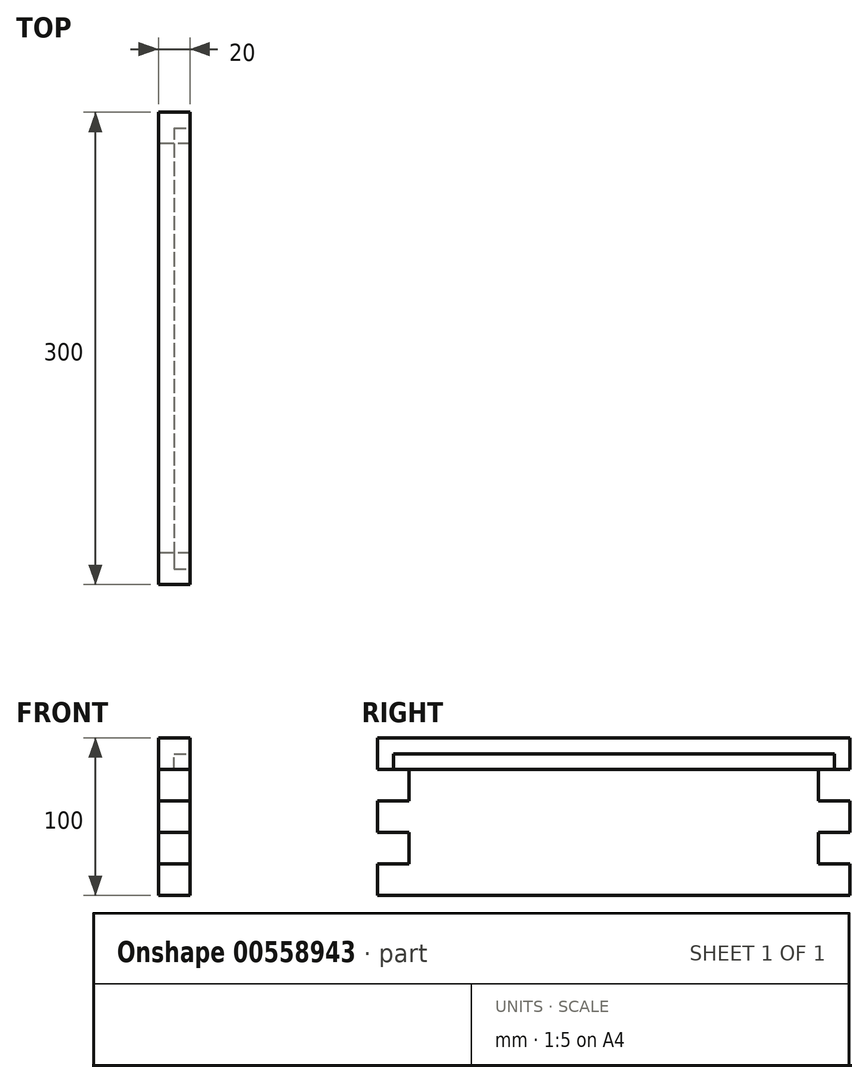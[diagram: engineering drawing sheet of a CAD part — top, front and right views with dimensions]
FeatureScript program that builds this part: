
annotation { "Feature Type Name" : "Feature", "Feature Type Description" : "" }
export const myFeature = defineFeature(function(context is Context, id is Id, definition is map)
    precondition{}
    {
        {
            var Q0;
            Q0=qCreatedBy(makeId("Right.planeOp"),FACE);
            var sketch = newSketch(context, id + "F0", { "sketchPlane" : qUnion([Q0])});
            skLineSegment(sketch, "E0.bottom", {"start": v(150, -50) * mm, "end": v(-150, -50) * mm});
            skLineSegment(sketch, "E0.top", {"start": v(150, 50) * mm, "end": v(-150, 50) * mm});
            skLineSegment(sketch, "E0.left", {"start": v(150, -50) * mm, "end": v(150, 50) * mm});
            skLineSegment(sketch, "E0.right", {"start": v(-150, -50) * mm, "end": v(-150, 50) * mm});
            skPoint(sketch, "E0.middle", {"position": v(0, 0) * mm});
            skSolve(sketch);
        }
        {
            var Q0;
            Q0=makeQuery(id+"F0.imprint","IMPRINT",FACE,{"disambiguationData":[TD([[makeQuery(id+"F0.imprint","IMPRINT",EDGE,{"derivedFrom":sQuery(id+"F0.wireOp",EDGE,"E0.bottom")}),-1.0]])]});
            extrude(context, id + "F1", {"entities" : qUnion([Q0]), "depth" : 20 * mm, "offsetDistance" : 25 * mm});
        }
        {
            var Q0;
            Q0=makeQuery(id+"F1.opExtrude","CAP_FACE",FACE,{"disambiguationData":[OSD([sQuery(id+"F0.wireOp",EDGE,"E0.bottom"),sQuery(id+"F0.wireOp",EDGE,"E0.top"),sQuery(id+"F0.wireOp",EDGE,"E0.left"),sQuery(id+"F0.wireOp",EDGE,"E0.right")])],"isStart":true});
            var sketch = newSketch(context, id + "F2", { "sketchPlane" : qUnion([Q0])});
            skLineSegment(sketch, "E1.bottom", {"start": v(150, -30) * mm, "end": v(130, -30) * mm});
            skLineSegment(sketch, "E1.top", {"start": v(150, -10) * mm, "end": v(130, -10) * mm});
            skLineSegment(sketch, "E1.left", {"start": v(150, -30) * mm, "end": v(150, -10) * mm});
            skLineSegment(sketch, "E1.right", {"start": v(130, -30) * mm, "end": v(130, -10) * mm});
            skLineSegment(sketch, "E2.MirrorCS", {"start": v(-130, -30) * mm, "end": v(-130, -10) * mm});
            skLineSegment(sketch, "E3.MirrorCS", {"start": v(-150, -30) * mm, "end": v(-150, -10) * mm});
            skLineSegment(sketch, "E4.MirrorCS", {"start": v(-150, -10) * mm, "end": v(-130, -10) * mm});
            skLineSegment(sketch, "E5.MirrorCS", {"start": v(-150, -30) * mm, "end": v(-130, -30) * mm});
            skLineSegment(sketch, "E6.bottom", {"start": v(150, 10) * mm, "end": v(130, 10) * mm});
            skLineSegment(sketch, "E6.top", {"start": v(150, 30) * mm, "end": v(130, 30) * mm});
            skLineSegment(sketch, "E6.left", {"start": v(150, 10) * mm, "end": v(150, 30) * mm});
            skLineSegment(sketch, "E6.right", {"start": v(130, 10) * mm, "end": v(130, 30) * mm});
            skLineSegment(sketch, "E7.MirrorCS", {"start": v(-150, 10) * mm, "end": v(-150, 30) * mm});
            skLineSegment(sketch, "E8.MirrorCS", {"start": v(-130, 10) * mm, "end": v(-130, 30) * mm});
            skLineSegment(sketch, "E9.MirrorCS", {"start": v(-150, 10) * mm, "end": v(-130, 10) * mm});
            skLineSegment(sketch, "E10.MirrorCS", {"start": v(-150, 30) * mm, "end": v(-130, 30) * mm});
            skSolve(sketch);
        }
        {
            var Q0;
            Q0 = qSketchRegion(id + "F2", true);
            extrude(context, id + "F3", {"entities" : qUnion([Q0]), "operationType" : NewBodyOperationType.REMOVE, "endBound" : BoundingType.UP_TO_NEXT, "oppositeDirection" : true, "depth" : 25 * mm, "offsetDistance" : 25 * mm});
        }
        {
            var Q0;
            Q0=makeQuery(id+"F1.opExtrude","CAP_FACE",FACE,{"disambiguationData":[OSD([sQuery(id+"F0.wireOp",EDGE,"E0.bottom"),sQuery(id+"F0.wireOp",EDGE,"E0.top"),sQuery(id+"F0.wireOp",EDGE,"E0.left"),sQuery(id+"F0.wireOp",EDGE,"E0.right")])],"isStart":false});
            var sketch = newSketch(context, id + "F4", { "sketchPlane" : qUnion([Q0])});
            skLineSegment(sketch, "E11.bottom", {"start": v(140, 30) * mm, "end": v(-140, 30) * mm});
            skLineSegment(sketch, "E11.top", {"start": v(140, 40) * mm, "end": v(-140, 40) * mm});
            skLineSegment(sketch, "E11.left", {"start": v(140, 30) * mm, "end": v(140, 40) * mm});
            skLineSegment(sketch, "E11.right", {"start": v(-140, 30) * mm, "end": v(-140, 40) * mm});
            skPoint(sketch, "E11.middle", {"position": v(0, 35) * mm});
            skSolve(sketch);
        }
        {
            var Q0;
            Q0 = qSketchRegion(id + "F4", true);
            extrude(context, id + "F5", {"entities" : qUnion([Q0]), "operationType" : NewBodyOperationType.REMOVE, "oppositeDirection" : true, "depth" : 10 * mm, "offsetDistance" : 25 * mm});
        }
    });
